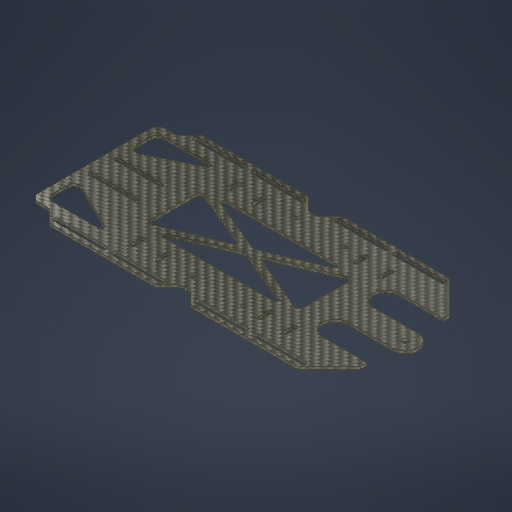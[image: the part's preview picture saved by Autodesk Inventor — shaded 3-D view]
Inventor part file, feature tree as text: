
AUTODESK INVENTOR PART (.ipt)
format: ipt  version: 2025 (Build 290162010, 162A)  size: 706,048 bytes
history: native  units: mm
features: extrude x7, sketch x7, fillet x1
ambient origin geometry x8: Origin, YZ Plane, XZ Plane, XY Plane, X Axis, Y Axis, Z Axis, Center Point
bodies: Solid1 (feature_tree)
feature tree (15):
  extrude  "Extrusion1"  Depth=73.0mm
  extrude  "Extrusion2"  Depth=58.0mm
  extrude  "Extrusion3"  Depth=50.0mm
  fillet  "Fillet1"  Radius=10.0mm
  extrude  "Extrusion4"  Depth=20.0mm
  extrude  "Extrusion5"  Depth=3.0mm
  extrude  "Extrusion6"  Depth=245.0mm
  extrude  "Extrusion7"  Depth=2.0mm TaperAngle=0.0deg
  sketch  "Sketch1"  dims[d0=220.0mm d1=73.0mm]
  sketch  "Sketch2"  dims[d2=190.0mm d3=58.0mm]
  sketch  "Sketch3"  dims[d4=5.0mm d5=50.0mm d6=10.0mm]
  sketch  "Sketch5"  dims[d7=20.0mm d8=7.5mm]
  sketch  "Sketch6"  dims[d9=3.0mm d10=7.5mm]
  sketch  "Sketch7"  dims[d11=3.0mm d12=245.0mm]
  sketch  "Sketch8"  dims[d13=100.0mm d14=2.0mm d15=0.0mm d16=80.0mm d17=20.0mm d18=7.5mm d19=3.0mm d20=7.5mm d21=3.0mm d22=10.0mm d23=10.0mm d24=35.0mm d25=3.0mm d26=35.0mm d27=3.0mm d28=55.5mm d29=55.0mm d30=4.0mm d31=37.5mm d32=3.5mm d36=30.0mm d37=15.0mm d38=10.0mm d39=10.0mm d40=5.0mm d41=2.0mm d42=0.0mm d43=45.0mm d44=45.0deg d45=45.0mm d46=45.0deg d49=1.0mm d50=0.0mm d51=6.0mm d52=20.0mm d53=35.0mm d54=35.0mm d55=20.0mm d56=20.0mm d57=35.0mm d58=20.0mm d59=35.0mm d60=20.0mm d61=15.0mm d62=40.0mm d63=80.0mm d64=3.5mm d65=3.5mm d66=3.5mm d67=3.5mm d68=1.0mm d69=0.0mm d70=25.0mm d71=4.7mm d72=1.0mm d73=0.0mm d76=120.0mm d77=50.0mm d78=2.5mm d79=2.5mm d80=2.5mm d81=2.5mm d82=3.0mm d83=2.0mm d84=5.0mm d85=3.0mm d86=0.0mm d87=50.0mm d88=25.0mm d89=50.0mm d90=25.0mm d91=5.0mm d92=5.0mm d93=2.0mm d94=3.0mm d95=0.0mm d47=0.5mm d48=0.872665mm d74=0.5mm d75=0.872665mm]
